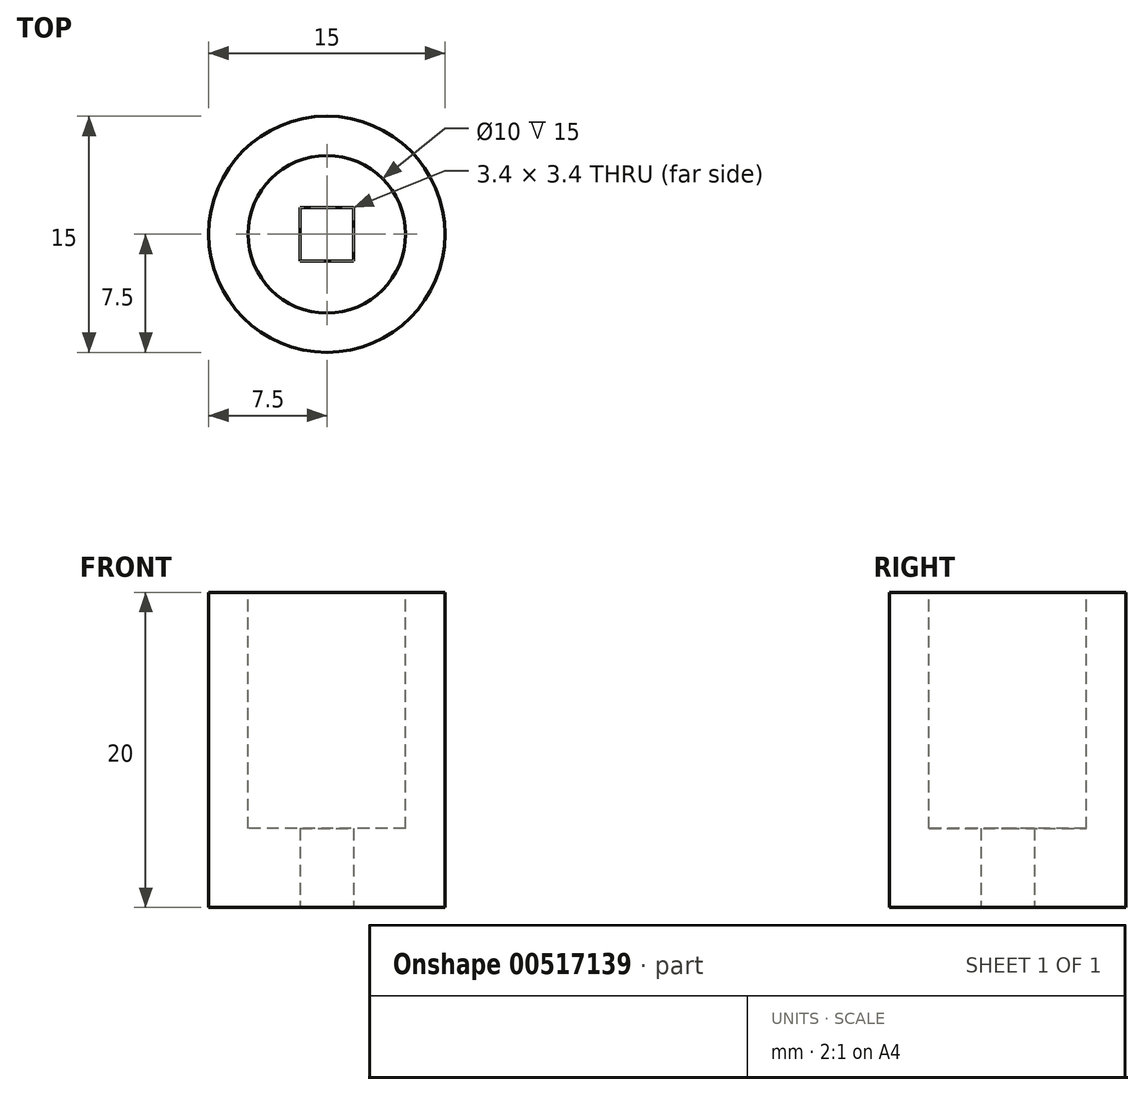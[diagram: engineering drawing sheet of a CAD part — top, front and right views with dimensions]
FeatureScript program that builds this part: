
annotation { "Feature Type Name" : "Feature", "Feature Type Description" : "" }
export const myFeature = defineFeature(function(context is Context, id is Id, definition is map)
    precondition{}
    {
        {
            var Q0;
            Q0=qCreatedBy(makeId("Top.planeOp"),FACE);
            var sketch = newSketch(context, id + "F0", { "sketchPlane" : qUnion([Q0])});
            skCircle(sketch, "E0", {"center": v(0, 0) * mm, "radius": 7.5 * mm});
            skSolve(sketch);
        }
        {
            var Q0;
            Q0 = qSketchRegion(id + "F0", true);
            extrude(context, id + "F1", {"entities" : qUnion([Q0]), "depth" : 20 * mm, "offsetDistance" : 25 * mm});
        }
        {
            var Q0;
            Q0=makeQuery(id+"F1.opExtrude","CAP_FACE",FACE,{"disambiguationData":[OSD([sQuery(id+"F0.wireOp",EDGE,"E0")])],"isStart":false});
            var sketch = newSketch(context, id + "F2", { "sketchPlane" : qUnion([Q0])});
            skCircle(sketch, "E1", {"center": v(0, 0) * mm, "radius": 5 * mm});
            skSolve(sketch);
        }
        {
            var Q0;
            Q0=makeQuery(id+"F2.imprint","IMPRINT",FACE,{"disambiguationData":[TD([[makeQuery(id+"F2.imprint","IMPRINT",EDGE,{"derivedFrom":sQuery(id+"F2.wireOp",EDGE,"E1")}),1.0]])]});
            extrude(context, id + "F3", {"entities" : qUnion([Q0]), "operationType" : NewBodyOperationType.REMOVE, "oppositeDirection" : true, "depth" : 15 * mm, "offsetDistance" : 25 * mm});
        }
        {
            var Q0;
            Q0=makeQuery(id+"F1.opExtrude","CAP_FACE",FACE,{"disambiguationData":[OSD([sQuery(id+"F0.wireOp",EDGE,"E0")])],"isStart":true});
            var sketch = newSketch(context, id + "F4", { "sketchPlane" : qUnion([Q0])});
            skLineSegment(sketch, "E2.bottom", {"start": v(1.7, 1.7) * mm, "end": v(-1.7, 1.7) * mm});
            skLineSegment(sketch, "E2.top", {"start": v(1.7, -1.7) * mm, "end": v(-1.7, -1.7) * mm});
            skLineSegment(sketch, "E2.left", {"start": v(1.7, 1.7) * mm, "end": v(1.7, -1.7) * mm});
            skLineSegment(sketch, "E2.right", {"start": v(-1.7, 1.7) * mm, "end": v(-1.7, -1.7) * mm});
            skPoint(sketch, "E2.middle", {"position": v(0, 0) * mm});
            skSolve(sketch);
        }
        {
            var Q0;
            Q0=makeQuery(id+"F4.imprint","IMPRINT",FACE,{"disambiguationData":[TD([[makeQuery(id+"F4.imprint","IMPRINT",EDGE,{"derivedFrom":sQuery(id+"F4.wireOp",EDGE,"E2.bottom")}),1.0]])]});
            extrude(context, id + "F5", {"entities" : qUnion([Q0]), "operationType" : NewBodyOperationType.REMOVE, "oppositeDirection" : true, "depth" : 10 * mm, "offsetDistance" : 25 * mm});
        }
    });
